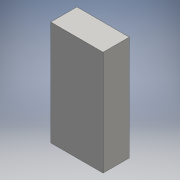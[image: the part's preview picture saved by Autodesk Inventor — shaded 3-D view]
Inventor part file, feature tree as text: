
AUTODESK INVENTOR PART (.ipt)
format: ipt  version: 2016 (Build 200138000, 138)  size: 84,992 bytes
history: native  units: mm
features: other x1, extrude x1, sketch x1
ambient origin geometry x8: Origin, YZ Plane, XZ Plane, XY Plane, X Axis, Y Axis, Z Axis, Center Point
bodies: Body1 (feature_tree)
feature tree (3):
  other  "ソリッド1"
  extrude  "押し出し1"  Depth=10.0mm
  sketch  "スケッチ1"
